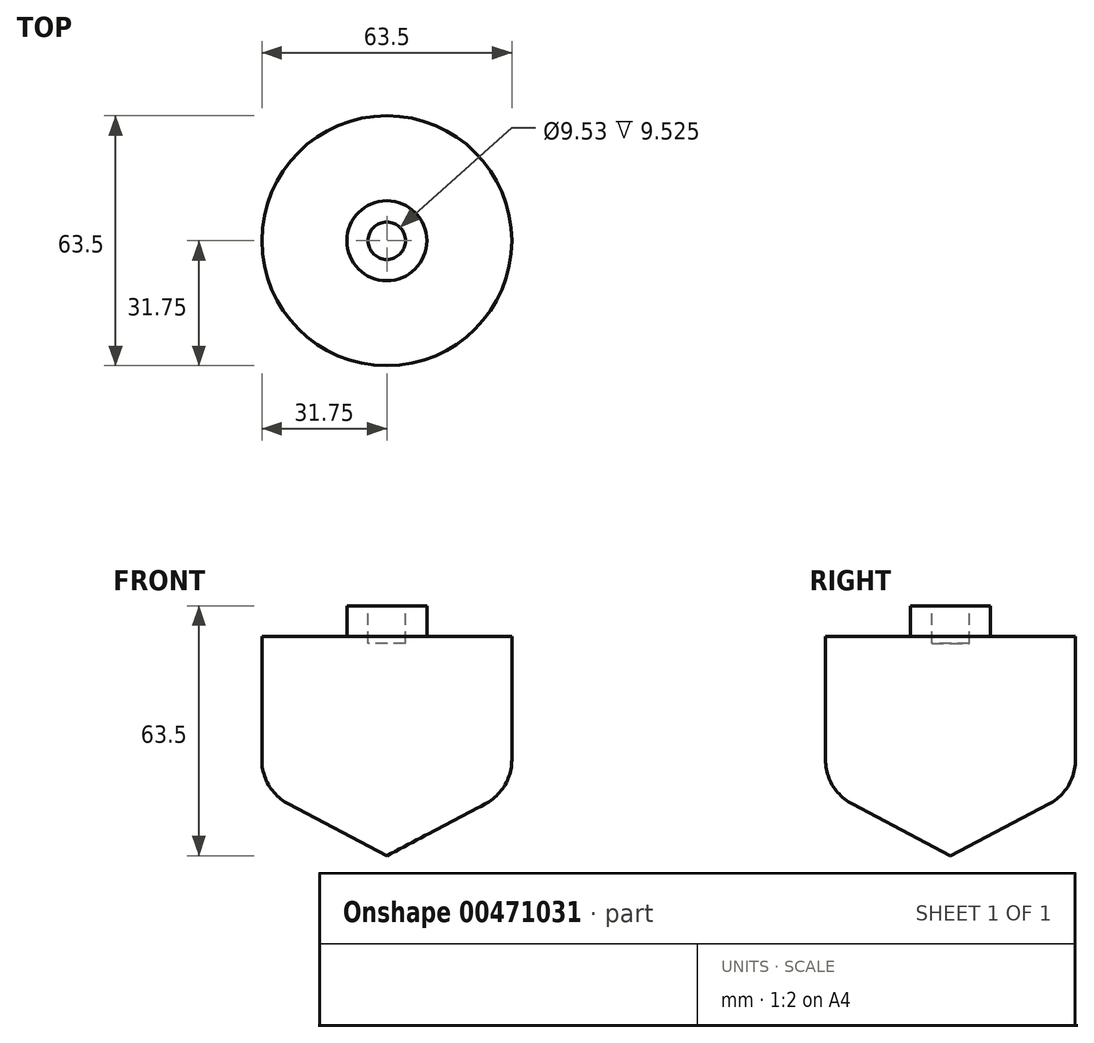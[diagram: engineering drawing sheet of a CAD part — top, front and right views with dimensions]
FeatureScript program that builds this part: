
annotation { "Feature Type Name" : "Feature", "Feature Type Description" : "" }
export const myFeature = defineFeature(function(context is Context, id is Id, definition is map)
    precondition{}
    {
        {
            var Q0;
            Q0=qCreatedBy(makeId("Front.planeOp"),FACE);
            var sketch = newSketch(context, id + "F0", { "sketchPlane" : qUnion([Q0])});
            skLineSegment(sketch, "E0", {"start": v(10.16, 63.5) * mm, "end": v(0, 63.5) * mm});
            skLineSegment(sketch, "E1", {"start": v(0, 63.5) * mm, "end": v(0, 0) * mm});
            skLineSegment(sketch, "E2", {"start": v(31.75, 28.87) * mm, "end": v(31.75, 46.2) * mm});
            skLineSegment(sketch, "E3", {"start": v(0, 0) * mm, "end": v(31.75, 16.69) * mm});
            skLineSegment(sketch, "E4", {"start": v(31.75, 46.2) * mm, "end": v(31.75, 28.87) * mm});
            skLineSegment(sketch, "E5", {"start": v(31.75, 46.2) * mm, "end": v(31.75, 55.76) * mm});
            skLineSegment(sketch, "E6", {"start": v(31.75, 55.76) * mm, "end": v(10.16, 55.76) * mm});
            skLineSegment(sketch, "E7", {"start": v(10.16, 55.76) * mm, "end": v(10.16, 63.5) * mm});
            skLineSegment(sketch, "E8", {"start": v(31.75, 28.87) * mm, "end": v(31.75, 16.69) * mm});
            skSolve(sketch);
        }
        {
            var Q0;
            Q0=qSketchRegion(id+"F0",true);
            var Q1;
            Q1=sQuery(id+"F0.wireOp",EDGE,"E1");
            revolve(context, id + "F1", {"entities" : qUnion([Q0]), "axis" : qUnion([Q1]), "revolveType" : RevolveType.FULL});
        }
        {
            var Q0;
            Q0=makeQuery(id+"F1.opRevolve","SWEPT_FACE",FACE,{"disambiguationData":[OSD([sQuery(id+"F0.wireOp",EDGE,"E0")])]});
            var sketch = newSketch(context, id + "F2", { "sketchPlane" : qUnion([Q0])});
            skCircle(sketch, "E9", {"center": v(0, 0) * mm, "radius": 4.76 * mm});
            skCircle(sketch, "E10", {"center": v(0, -63.96) * mm, "radius": 1.59 * mm});
            skSolve(sketch);
        }
        {
            var Q0;
            Q0=makeQuery(id+"F2.imprint","IMPRINT",FACE,{"disambiguationData":[TD([[makeQuery(id+"F2.imprint","IMPRINT",EDGE,{"derivedFrom":sQuery(id+"F2.wireOp",EDGE,"E9")}),1.0]])]});
            extrude(context, id + "F3", {"entities" : qUnion([Q0]), "operationType" : NewBodyOperationType.REMOVE, "oppositeDirection" : true, "depth" : 9.52 * mm});
        }
        {
            var Q0;
            Q0=qCreatedBy(makeId("Top.planeOp"),FACE);
            var sketch = newSketch(context, id + "F4", { "sketchPlane" : qUnion([Q0])});
            skCircle(sketch, "E11", {"center": v(0, 0) * mm, "radius": 1.59 * mm});
            skSolve(sketch);
        }
        {
            var Q0;
            Q0=makeQuery(id+"F1.opRevolve","SWEPT_EDGE",EDGE,{"disambiguationData":[OSD([sQuery(id+"F0.wireOp",EDGE,"E3"),sQuery(id+"F0.wireOp",EDGE,"E8")])]});
            fillet(context, id + "F5", {"entities" : qUnion([Q0]), "radius" : 12.7 * mm, "tangentPropagation" : true, "allowEdgeOverflow" : false});
        }
        {
            var Q0;
            Q0=sQuery(id+"F4.wireOp",EDGE,"E11");
            extrude(context, id + "F6", {"bodyType" : ToolBodyType.SURFACE, "surfaceEntities" : qUnion([Q0]), "depth" : 14.3 * mm});
        }
    });
